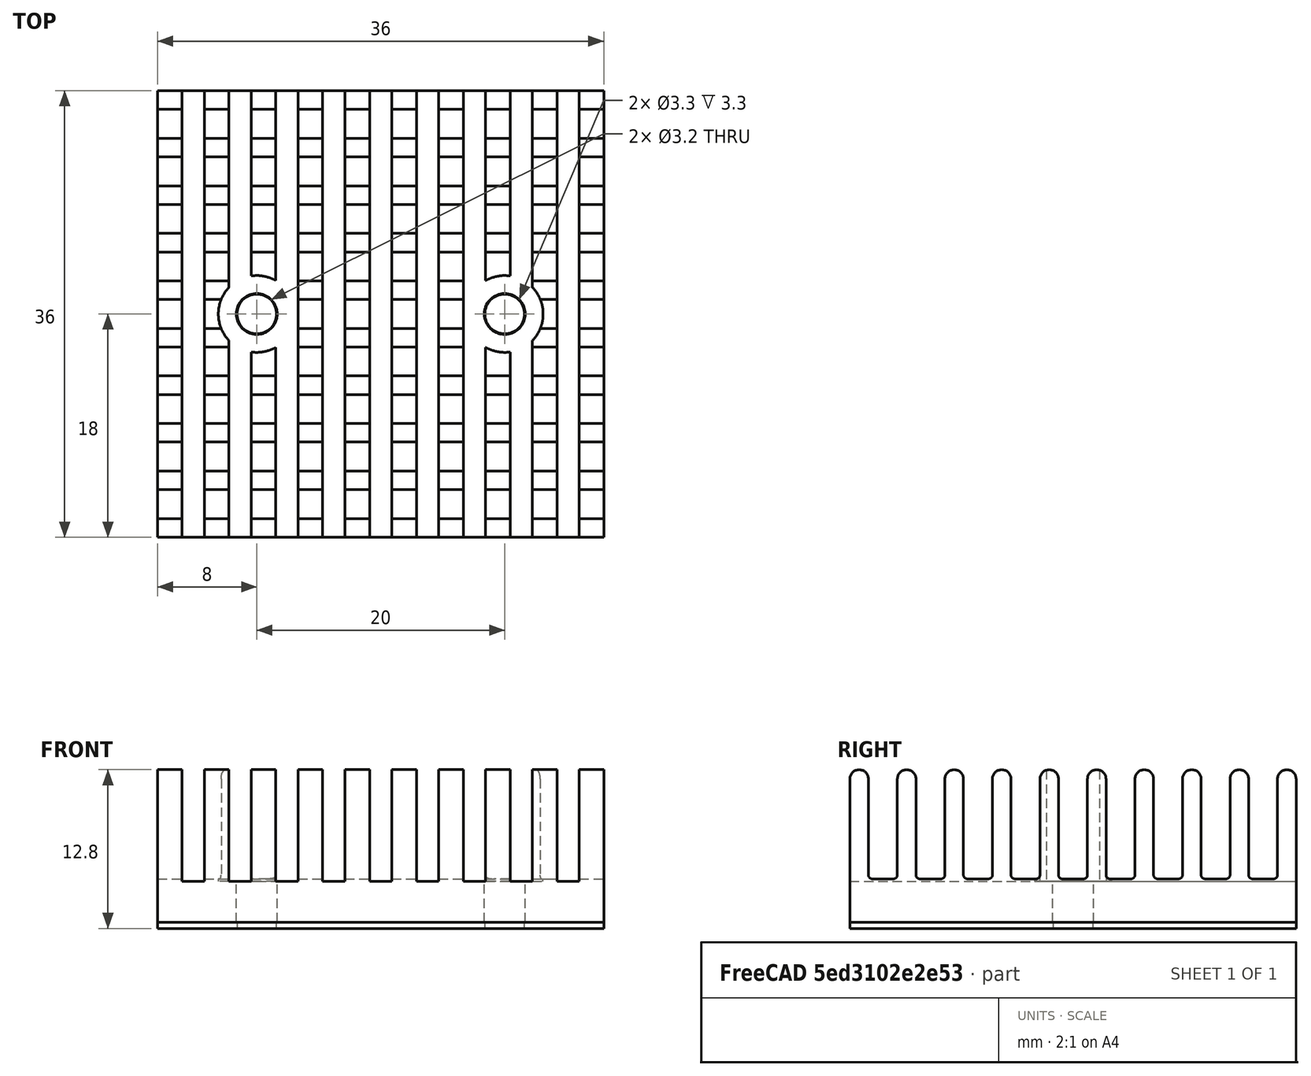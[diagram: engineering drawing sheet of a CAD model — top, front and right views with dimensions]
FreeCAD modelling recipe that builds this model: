
FCSTD DOCUMENT  (FreeCAD 0.19R)
Label: HeatSink_FischerElektronik__ICK_PGA_14_x_14_x_12
License: All rights reserved
LicenseURL: http://en.wikipedia.org/wiki/All_rights_reserved
objects: TechDraw::DrawViewDimension×11, Sketcher::SketchObject×8, App::Part×4, TechDraw::DrawProjGroupItem×4, PartDesign::Pad×3, PartDesign::Pocket×3, PartDesign::Body×3, PartDesign::Hole×2, TechDraw::DrawSVGTemplate×2, TechDraw::DrawViewAnnotation×2, TechDraw::DrawPage×2, PartDesign::Fillet×1, TechDraw::DrawProjGroup×1, TechDraw::DrawViewSection×1, TechDraw::DrawViewPart×1, PartDesign::FeatureBase×1, TechDraw::DrawViewImage×1
note: 30 computed .brp shape members not serialized (recipe doc carries the construction recipe); baked Part::Feature solids carry a one-line shape summary decoded from their .brp

FEATURE [Sketcher::SketchObject] Sketch  label="Sketch_profile"
  MapMode = 5
  Placement = pos=(0,0,0) rot=(0.57735,0.57735,0.57735;2.0944rad)
  Support = -> [YZ_Plane001]
  sketch-geometry (59):
    g0: LineSegment StartX=-18 StartY=0 StartZ=0 EndX=18 EndY=0 EndZ=0
    g1: ArcOfCircle CenterX=-17.25 CenterY=11.55 CenterZ=0 NormalX=0 NormalY=0 NormalZ=1 AngleXU=0 Radius=0.75 StartAngle=1.09717e-07 EndAngle=3.14159
    g2: LineSegment StartX=-16.5 StartY=11.55 StartZ=0 EndX=-16.5 EndY=3.5 EndZ=0
    g3: LineSegment StartX=-16.5 StartY=3.5 StartZ=0 EndX=-14.1667 EndY=3.5 EndZ=0
    g4: LineSegment StartX=-18 StartY=11.55 StartZ=0 EndX=-18 EndY=0 EndZ=0
    g5: LineSegment [constr] StartX=-17.25 StartY=11.55 StartZ=0 EndX=-17.25 EndY=12.3 EndZ=0
    g6: ArcOfCircle CenterX=-13.4167 CenterY=11.55 CenterZ=0 NormalX=0 NormalY=0 NormalZ=1 AngleXU=0 Radius=0.75 StartAngle=6.1363e-08 EndAngle=3.14159
    g7: LineSegment StartX=-12.6667 StartY=11.55 StartZ=0 EndX=-12.6667 EndY=3.5 EndZ=0
    g8: LineSegment StartX=-12.6667 StartY=3.5 StartZ=0 EndX=-10.3333 EndY=3.5 EndZ=0
    g9: LineSegment StartX=-14.1667 StartY=11.55 StartZ=0 EndX=-14.1667 EndY=3.5 EndZ=0
    g10: LineSegment [constr] StartX=-13.4167 StartY=11.55 StartZ=0 EndX=-13.4167 EndY=12.3 EndZ=0
    g11: LineSegment [constr] StartX=-16.5 StartY=11.55 StartZ=0 EndX=-12.6667 EndY=11.55 EndZ=0
    g12: ArcOfCircle CenterX=-9.58333 CenterY=11.55 CenterZ=0 NormalX=0 NormalY=0 NormalZ=1 AngleXU=0 Radius=0.75 StartAngle=6.28319 EndAngle=9.42478
    g13: LineSegment StartX=-8.83333 StartY=11.55 StartZ=0 EndX=-8.83333 EndY=3.5 EndZ=0
    g14: LineSegment StartX=-8.83333 StartY=3.5 StartZ=0 EndX=-6.5 EndY=3.5 EndZ=0
    g15: LineSegment StartX=-10.3333 StartY=11.55 StartZ=0 EndX=-10.3333 EndY=3.5 EndZ=0
    g16: LineSegment [constr] StartX=-9.58333 StartY=11.55 StartZ=0 EndX=-9.58333 EndY=12.3 EndZ=0
    g17: LineSegment [constr] StartX=-12.6667 StartY=11.55 StartZ=0 EndX=-8.83333 EndY=11.55 EndZ=0
    g18: ArcOfCircle CenterX=-5.75 CenterY=11.55 CenterZ=0 NormalX=0 NormalY=0 NormalZ=1 AngleXU=0 Radius=0.75 StartAngle=6.28319 EndAngle=9.42478
    g19: LineSegment StartX=-5 StartY=11.55 StartZ=0 EndX=-5 EndY=3.5 EndZ=0
    g20: LineSegment StartX=-5 StartY=3.5 StartZ=0 EndX=-2.66667 EndY=3.5 EndZ=0
    g21: LineSegment StartX=-6.5 StartY=11.55 StartZ=0 EndX=-6.5 EndY=3.5 EndZ=0
    g22: LineSegment [constr] StartX=-5.75 StartY=11.55 StartZ=0 EndX=-5.75 EndY=12.3 EndZ=0
    g23: LineSegment [constr] StartX=-8.83333 StartY=11.55 StartZ=0 EndX=-5 EndY=11.55 EndZ=0
    g24: ArcOfCircle CenterX=-1.91667 CenterY=11.55 CenterZ=0 NormalX=0 NormalY=0 NormalZ=1 AngleXU=0 Radius=0.75 StartAngle=5.6678e-08 EndAngle=3.14159
    g25: LineSegment StartX=-1.16667 StartY=11.55 StartZ=0 EndX=-1.16667 EndY=3.5 EndZ=0
    g26: LineSegment StartX=-1.16667 StartY=3.5 StartZ=0 EndX=1.16667 EndY=3.5 EndZ=0
    g27: LineSegment StartX=-2.66667 StartY=11.55 StartZ=0 EndX=-2.66667 EndY=3.5 EndZ=0
    g28: LineSegment [constr] StartX=-1.91667 StartY=11.55 StartZ=0 EndX=-1.91667 EndY=12.3 EndZ=0
    g29: LineSegment [constr] StartX=-5 StartY=11.55 StartZ=0 EndX=-1.16667 EndY=11.55 EndZ=0
    g30: ArcOfCircle CenterX=1.91667 CenterY=11.55 CenterZ=0 NormalX=0 NormalY=0 NormalZ=1 AngleXU=0 Radius=0.75 StartAngle=4.771e-09 EndAngle=3.14159
    g31: LineSegment StartX=2.66667 StartY=11.55 StartZ=0 EndX=2.66667 EndY=3.5 EndZ=0
    g32: LineSegment StartX=2.66667 StartY=3.5 StartZ=0 EndX=5 EndY=3.5 EndZ=0
    g33: LineSegment StartX=1.16667 StartY=11.55 StartZ=0 EndX=1.16667 EndY=3.5 EndZ=0
    g34: LineSegment [constr] StartX=1.91667 StartY=11.55 StartZ=0 EndX=1.91667 EndY=12.3 EndZ=0
    g35: LineSegment [constr] StartX=-1.16667 StartY=11.55 StartZ=0 EndX=2.66667 EndY=11.55 EndZ=0
    g36: ArcOfCircle CenterX=5.75 CenterY=11.55 CenterZ=0 NormalX=0 NormalY=0 NormalZ=1 AngleXU=0 Radius=0.75 StartAngle=2.3161e-08 EndAngle=3.1416
    g37: LineSegment StartX=6.5 StartY=11.55 StartZ=0 EndX=6.5 EndY=3.5 EndZ=0
    g38: LineSegment StartX=6.5 StartY=3.5 StartZ=0 EndX=8.83333 EndY=3.5 EndZ=0
    g39: LineSegment StartX=5 StartY=11.55 StartZ=0 EndX=5 EndY=3.5 EndZ=0
    g40: LineSegment [constr] StartX=5.75 StartY=11.55 StartZ=0 EndX=5.75 EndY=12.3 EndZ=0
    g41: LineSegment [constr] StartX=2.66667 StartY=11.55 StartZ=0 EndX=6.5 EndY=11.55 EndZ=0
    g42: ArcOfCircle CenterX=9.58333 CenterY=11.55 CenterZ=0 NormalX=0 NormalY=0 NormalZ=1 AngleXU=0 Radius=0.75 StartAngle=6.28319 EndAngle=9.42478
    g43: LineSegment StartX=10.3333 StartY=11.55 StartZ=0 EndX=10.3333 EndY=3.5 EndZ=0
    g44: LineSegment StartX=10.3333 StartY=3.5 StartZ=0 EndX=12.6667 EndY=3.5 EndZ=0
    g45: LineSegment StartX=8.83333 StartY=11.55 StartZ=0 EndX=8.83333 EndY=3.5 EndZ=0
    g46: LineSegment [constr] StartX=9.58333 StartY=11.55 StartZ=0 EndX=9.58333 EndY=12.3 EndZ=0
    g47: LineSegment [constr] StartX=6.5 StartY=11.55 StartZ=0 EndX=10.3333 EndY=11.55 EndZ=0
    g48: ArcOfCircle CenterX=13.4167 CenterY=11.55 CenterZ=0 NormalX=0 NormalY=0 NormalZ=1 AngleXU=0 Radius=0.75 StartAngle=8.3908e-08 EndAngle=3.14159
    g49: LineSegment StartX=14.1667 StartY=11.55 StartZ=0 EndX=14.1667 EndY=3.5 EndZ=0
    g50: LineSegment StartX=14.1667 StartY=3.5 StartZ=0 EndX=16.5 EndY=3.5 EndZ=0
    g51: LineSegment StartX=12.6667 StartY=11.55 StartZ=0 EndX=12.6667 EndY=3.5 EndZ=0
    g52: LineSegment [constr] StartX=13.4167 StartY=11.55 StartZ=0 EndX=13.4167 EndY=12.3 EndZ=0
    g53: LineSegment [constr] StartX=10.3333 StartY=11.55 StartZ=0 EndX=14.1667 EndY=11.55 EndZ=0
    g54: ArcOfCircle CenterX=17.25 CenterY=11.55 CenterZ=0 NormalX=0 NormalY=0 NormalZ=1 AngleXU=0 Radius=0.75 StartAngle=6.28319 EndAngle=9.42478
    g55: LineSegment StartX=18 StartY=11.55 StartZ=0 EndX=18 EndY=0 EndZ=0
    g56: LineSegment StartX=16.5 StartY=11.55 StartZ=0 EndX=16.5 EndY=3.5 EndZ=0
    g57: LineSegment [constr] StartX=17.25 StartY=11.55 StartZ=0 EndX=17.25 EndY=12.3 EndZ=0
    g58: LineSegment [constr] StartX=14.1667 StartY=11.55 StartZ=0 EndX=18 EndY=11.55 EndZ=0
  constraints (177):
    c: Horizontal(g0)
    c: Symmetric(g0,g0,g-1)
    c: DistanceX(g0,g0) = 36
    c: Vertical(g2)
    c: Coincident(g3,g2)
    c: Horizontal(g3)
    c: Coincident(g1,g2)
    c: Tangent(g1,g2)
    c: Coincident(g4,g1)
    c: Vertical(g4)
    c: Tangent(g4,g1)
    c: Vertical(g5)
    c: Coincident(g1,g5)
    c: PointOnObject(g5,g1)
    c: DistanceY(g0,g5) = 12.3
    c: DistanceY(g0,g2) = 3.5
    c: Radius(g1) = 0.75
    c: Vertical(g7)
    c: Coincident(g8,g7)
    c: Horizontal(g8)
    c: Coincident(g6,g7)
    c: Tangent(g6,g7)
    c: Coincident(g9,g6)
    c: Vertical(g9)
    c: Tangent(g9,g6)
    c: Equal(g9,g7)
    c: Vertical(g10)
    c: Coincident(g6,g10)
    c: PointOnObject(g10,g6)
    c: Equal(g1,g6) = 0.75
    c: Coincident(g1,g11)
    c: Coincident(g6,g11)
    c: Vertical(g13)
    c: Coincident(g14,g13)
    c: Horizontal(g14)
    c: Coincident(g12,g13)
    c: Tangent(g12,g13)
    c: Coincident(g15,g12)
    c: Vertical(g15)
    c: Tangent(g15,g12)
    c: Equal(g15,g13)
    c: Vertical(g16)
    c: Coincident(g12,g16)
    c: PointOnObject(g16,g12)
    c: Equal(g1,g12) = 0.75
    c: Coincident(g6,g17)
    c: Coincident(g12,g17)
    c: Equal(g11,g17)
    c: Parallel(g17,g11)
    c: Vertical(g19)
    c: Coincident(g20,g19)
    c: Horizontal(g20)
    c: Coincident(g18,g19)
    c: Tangent(g18,g19)
    c: Coincident(g21,g18)
    c: Vertical(g21)
    c: Tangent(g21,g18)
    c: Equal(g21,g19)
    c: Vertical(g22)
    c: Coincident(g18,g22)
    c: PointOnObject(g22,g18)
    c: Equal(g1,g18) = 0.75
    c: Coincident(g12,g23)
    c: Coincident(g18,g23)
    c: Equal(g11,g23)
    c: Parallel(g23,g11)
    c: Vertical(g25)
    c: Coincident(g26,g25)
    c: Horizontal(g26)
    c: Coincident(g24,g25)
    c: Tangent(g24,g25)
    c: Coincident(g27,g24)
    c: Vertical(g27)
    c: Tangent(g27,g24)
    c: Equal(g27,g25)
    c: Vertical(g28)
    c: Coincident(g24,g28)
    c: PointOnObject(g28,g24)
    c: Equal(g1,g24) = 0.75
    c: Coincident(g18,g29)
    c: Coincident(g24,g29)
    c: Equal(g11,g29)
    c: Parallel(g29,g11)
    c: Vertical(g31)
    c: Coincident(g32,g31)
    c: Horizontal(g32)
    c: Coincident(g30,g31)
    c: Tangent(g30,g31)
    c: Coincident(g33,g30)
    c: Vertical(g33)
    c: Tangent(g33,g30)
    c: Equal(g33,g31)
    c: Vertical(g34)
    c: Coincident(g30,g34)
    c: PointOnObject(g34,g30)
    c: Equal(g1,g30) = 0.75
    c: Coincident(g24,g35)
    c: Coincident(g30,g35)
    c: Equal(g11,g35)
    c: Parallel(g35,g11)
    c: Vertical(g37)
    c: Coincident(g38,g37)
    c: Horizontal(g38)
    c: Coincident(g36,g37)
    c: Tangent(g36,g37)
    c: Coincident(g39,g36)
    c: Vertical(g39)
    c: Tangent(g39,g36)
    c: Equal(g39,g37)
    c: Vertical(g40)
    c: Coincident(g36,g40)
    c: PointOnObject(g40,g36)
    c: Equal(g1,g36) = 0.75
    c: Coincident(g30,g41)
    c: Coincident(g36,g41)
    c: Equal(g11,g41)
    c: Parallel(g41,g11)
    c: Vertical(g43)
    c: Coincident(g44,g43)
    c: Horizontal(g44)
    c: Coincident(g42,g43)
    c: Tangent(g42,g43)
    c: Coincident(g45,g42)
    c: Vertical(g45)
    c: Tangent(g45,g42)
    c: Equal(g45,g43)
    c: Vertical(g46)
    c: Coincident(g42,g46)
    c: PointOnObject(g46,g42)
    c: Equal(g1,g42) = 0.75
    c: Coincident(g36,g47)
    c: Coincident(g42,g47)
    c: Equal(g11,g47)
    c: Parallel(g47,g11)
    c: Vertical(g49)
    c: Coincident(g50,g49)
    c: Horizontal(g50)
    c: Coincident(g48,g49)
    c: Tangent(g48,g49)
    c: Coincident(g51,g48)
    c: Vertical(g51)
    c: Tangent(g51,g48)
    c: Equal(g51,g49)
    c: Vertical(g52)
    c: Coincident(g48,g52)
    c: PointOnObject(g52,g48)
    c: Equal(g1,g48) = 0.75
    c: Coincident(g42,g53)
    c: Coincident(g48,g53)
    c: Equal(g11,g53)
    c: Parallel(g53,g11)
    c: Vertical(g55)
    c: Coincident(g54,g55)
    c: Tangent(g54,g55)
    c: Coincident(g56,g54)
    c: Vertical(g56)
    c: Tangent(g56,g54)
    c: Vertical(g57)
    c: Coincident(g54,g57)
    c: PointOnObject(g57,g54)
    c: Equal(g1,g54) = 0.75
    c: Coincident(g48,g58)
    c: Coincident(g54,g58)
    c: Equal(g11,g58)
    c: Parallel(g58,g11)
    c: Horizontal(g11)
    c: Coincident(g3,g9)
    c: Coincident(g8,g15)
    c: Coincident(g14,g21)
    c: Coincident(g20,g27)
    c: Coincident(g26,g33)
    c: Coincident(g32,g39)
    c: Coincident(g38,g45)
    c: Coincident(g44,g51)
    c: Coincident(g50,g56)
    c: Coincident(g55,g0)
    c: Coincident(g4,g0)
FEATURE [PartDesign::Pad] Pad  label="Pad_profile"
  AllowMultiFace = false
  Direction = (1,1,1)
  Length = 36
  Length2 = 100
  Midplane = true
  Placement = pos=(0,0,0) rot=(0.57735,0.57735,0.57735;2.0944rad)
  Profile = -> Sketch
  Type = 0
FEATURE [Sketcher::SketchObject] Sketch001  label="Sketch_cuts"
  ExternalGeometry = -> [Pad]
  MapMode = 5
  Placement = pos=(0,-18,2e-15) rot=(0.57735,0.57735,-0.57735;2.0944rad)
  Support = -> [Pad]
  sketch-geometry (47):
    g0: LineSegment StartX=-13.55 StartY=16.02 StartZ=0 EndX=-3.3 EndY=16.02 EndZ=0
    g1: LineSegment StartX=-3.3 StartY=16.02 StartZ=0 EndX=-3.3 EndY=14.22 EndZ=0
    g2: LineSegment StartX=-3.3 StartY=14.22 StartZ=0 EndX=-13.55 EndY=14.22 EndZ=0
    g3: LineSegment StartX=-13.55 StartY=14.22 StartZ=0 EndX=-13.55 EndY=16.02 EndZ=0
    g4: LineSegment [constr] StartX=-3.3 StartY=16.02 StartZ=0 EndX=-3.3 EndY=18 EndZ=0
    g5: LineSegment StartX=-13.55 StartY=12.24 StartZ=0 EndX=-3.3 EndY=12.24 EndZ=0
    g6: LineSegment StartX=-3.3 StartY=12.24 StartZ=0 EndX=-3.3 EndY=10.44 EndZ=0
    g7: LineSegment StartX=-3.3 StartY=10.44 StartZ=0 EndX=-13.55 EndY=10.44 EndZ=0
    g8: LineSegment StartX=-13.55 StartY=10.44 StartZ=0 EndX=-13.55 EndY=12.24 EndZ=0
    g9: LineSegment [constr] StartX=-13.55 StartY=16.02 StartZ=0 EndX=-13.55 EndY=12.24 EndZ=0
    g10: LineSegment StartX=-13.55 StartY=8.46 StartZ=0 EndX=-3.3 EndY=8.46 EndZ=0
    g11: LineSegment StartX=-3.3 StartY=8.46 StartZ=0 EndX=-3.3 EndY=6.66 EndZ=0
    g12: LineSegment StartX=-3.3 StartY=6.66 StartZ=0 EndX=-13.55 EndY=6.66 EndZ=0
    g13: LineSegment StartX=-13.55 StartY=6.66 StartZ=0 EndX=-13.55 EndY=8.46 EndZ=0
    g14: LineSegment [constr] StartX=-13.55 StartY=12.24 StartZ=0 EndX=-13.55 EndY=8.46 EndZ=0
    g15: LineSegment StartX=-13.55 StartY=4.68 StartZ=0 EndX=-3.3 EndY=4.68 EndZ=0
    g16: LineSegment StartX=-3.3 StartY=4.68 StartZ=0 EndX=-3.3 EndY=2.88 EndZ=0
    g17: LineSegment StartX=-3.3 StartY=2.88 StartZ=0 EndX=-13.55 EndY=2.88 EndZ=0
    g18: LineSegment StartX=-13.55 StartY=2.88 StartZ=0 EndX=-13.55 EndY=4.68 EndZ=0
    g19: LineSegment [constr] StartX=-13.55 StartY=8.46 StartZ=0 EndX=-13.55 EndY=4.68 EndZ=0
    g20: LineSegment StartX=-13.55 StartY=0.9 StartZ=0 EndX=-3.3 EndY=0.9 EndZ=0
    g21: LineSegment StartX=-3.3 StartY=0.9 StartZ=0 EndX=-3.3 EndY=-0.9 EndZ=0
    g22: LineSegment StartX=-3.3 StartY=-0.9 StartZ=0 EndX=-13.55 EndY=-0.9 EndZ=0
    g23: LineSegment StartX=-13.55 StartY=-0.9 StartZ=0 EndX=-13.55 EndY=0.9 EndZ=0
    g24: LineSegment [constr] StartX=-13.55 StartY=4.68 StartZ=0 EndX=-13.55 EndY=0.9 EndZ=0
    g25: LineSegment StartX=-13.55 StartY=-2.88 StartZ=0 EndX=-3.3 EndY=-2.88 EndZ=0
    g26: LineSegment StartX=-3.3 StartY=-2.88 StartZ=0 EndX=-3.3 EndY=-4.68 EndZ=0
    g27: LineSegment StartX=-3.3 StartY=-4.68 StartZ=0 EndX=-13.55 EndY=-4.68 EndZ=0
    g28: LineSegment StartX=-13.55 StartY=-4.68 StartZ=0 EndX=-13.55 EndY=-2.88 EndZ=0
    g29: LineSegment [constr] StartX=-13.55 StartY=0.9 StartZ=0 EndX=-13.55 EndY=-2.88 EndZ=0
    g30: LineSegment StartX=-13.55 StartY=-6.66 StartZ=0 EndX=-3.3 EndY=-6.66 EndZ=0
    g31: LineSegment StartX=-3.3 StartY=-6.66 StartZ=0 EndX=-3.3 EndY=-8.46 EndZ=0
    g32: LineSegment StartX=-3.3 StartY=-8.46 StartZ=0 EndX=-13.55 EndY=-8.46 EndZ=0
    g33: LineSegment StartX=-13.55 StartY=-8.46 StartZ=0 EndX=-13.55 EndY=-6.66 EndZ=0
    g34: LineSegment [constr] StartX=-13.55 StartY=-2.88 StartZ=0 EndX=-13.55 EndY=-6.66 EndZ=0
    g35: LineSegment StartX=-13.55 StartY=-10.44 StartZ=0 EndX=-3.3 EndY=-10.44 EndZ=0
    g36: LineSegment StartX=-3.3 StartY=-10.44 StartZ=0 EndX=-3.3 EndY=-12.24 EndZ=0
    g37: LineSegment StartX=-3.3 StartY=-12.24 StartZ=0 EndX=-13.55 EndY=-12.24 EndZ=0
    g38: LineSegment StartX=-13.55 StartY=-12.24 StartZ=0 EndX=-13.55 EndY=-10.44 EndZ=0
    g39: LineSegment [constr] StartX=-13.55 StartY=-6.66 StartZ=0 EndX=-13.55 EndY=-10.44 EndZ=0
    g40: LineSegment StartX=-13.55 StartY=-14.22 StartZ=0 EndX=-3.3 EndY=-14.22 EndZ=0
    g41: LineSegment StartX=-3.3 StartY=-14.22 StartZ=0 EndX=-3.3 EndY=-16.02 EndZ=0
    g42: LineSegment StartX=-3.3 StartY=-16.02 StartZ=0 EndX=-13.55 EndY=-16.02 EndZ=0
    g43: LineSegment StartX=-13.55 StartY=-16.02 StartZ=0 EndX=-13.55 EndY=-14.22 EndZ=0
    g44: LineSegment [constr] StartX=-13.55 StartY=-10.44 StartZ=0 EndX=-13.55 EndY=-14.22 EndZ=0
    g45: LineSegment [constr] StartX=-3.3 StartY=14.22 StartZ=0 EndX=-3.3 EndY=12.24 EndZ=0
    g46: LineSegment [constr] StartX=-3.3 StartY=-16.02 StartZ=0 EndX=-3.3 EndY=-18 EndZ=0
  constraints (132):
    c: Coincident(g0,g1)
    c: Coincident(g1,g2)
    c: Coincident(g2,g3)
    c: Coincident(g3,g0)
    c: Horizontal(g0)
    c: Horizontal(g2)
    c: Vertical(g1)
    c: Vertical(g3)
    c: DistanceX(g0,g-3) = 2
    c: DistanceX(g0,g-3) = 3.3
    c: Vertical(g4)
    c: Coincident(g0,g4)
    c: DistanceY(g1,g1) = 1.8
    c: PointOnObject(g4,g-3)
    c: Coincident(g5,g6)
    c: Coincident(g6,g7)
    c: Coincident(g7,g8)
    c: Coincident(g8,g5)
    c: Horizontal(g5)
    c: Horizontal(g7)
    c: Vertical(g6)
    c: Vertical(g8)
    c: Equal(g1,g6) = 1.8
    c: Coincident(g0,g9)
    c: Coincident(g5,g9)
    c: Coincident(g10,g11)
    c: Coincident(g11,g12)
    c: Coincident(g12,g13)
    c: Coincident(g13,g10)
    c: Horizontal(g10)
    c: Horizontal(g12)
    c: Vertical(g11)
    c: Vertical(g13)
    c: Equal(g1,g11) = 1.8
    c: Coincident(g5,g14)
    c: Coincident(g10,g14)
    c: Equal(g9,g14)
    c: Parallel(g14,g9)
    c: Coincident(g15,g16)
    c: Coincident(g16,g17)
    c: Coincident(g17,g18)
    c: Coincident(g18,g15)
    c: Horizontal(g15)
    c: Horizontal(g17)
    c: Vertical(g16)
    c: Vertical(g18)
    c: Equal(g1,g16) = 1.8
    c: Coincident(g10,g19)
    c: Coincident(g15,g19)
    c: Equal(g9,g19)
    c: Parallel(g19,g9)
    c: Coincident(g20,g21)
    c: Coincident(g21,g22)
    c: Coincident(g22,g23)
    c: Coincident(g23,g20)
    c: Horizontal(g20)
    c: Horizontal(g22)
    c: Vertical(g21)
    c: Vertical(g23)
    c: Equal(g1,g21) = 1.8
    c: Coincident(g15,g24)
    c: Coincident(g20,g24)
    c: Equal(g9,g24)
    c: Parallel(g24,g9)
    c: Coincident(g25,g26)
    c: Coincident(g26,g27)
    c: Coincident(g27,g28)
    c: Coincident(g28,g25)
    c: Horizontal(g25)
    c: Horizontal(g27)
    c: Vertical(g26)
    c: Vertical(g28)
    c: Equal(g1,g26) = 1.8
    c: Coincident(g20,g29)
    c: Coincident(g25,g29)
    c: Equal(g9,g29)
    c: Parallel(g29,g9)
    c: Coincident(g30,g31)
    c: Coincident(g31,g32)
    c: Coincident(g32,g33)
    c: Coincident(g33,g30)
    c: Horizontal(g30)
    c: Horizontal(g32)
    c: Vertical(g31)
    c: Vertical(g33)
    c: Equal(g1,g31) = 1.8
    c: Coincident(g25,g34)
    c: Coincident(g30,g34)
    c: Equal(g9,g34)
    c: Parallel(g34,g9)
    c: Coincident(g35,g36)
    c: Coincident(g36,g37)
    c: Coincident(g37,g38)
    c: Coincident(g38,g35)
    c: Horizontal(g35)
    c: Horizontal(g37)
    c: Vertical(g36)
    c: Vertical(g38)
    c: Equal(g1,g36) = 1.8
    c: Coincident(g30,g39)
    c: Coincident(g35,g39)
    c: Equal(g9,g39)
    c: Parallel(g39,g9)
    c: Coincident(g40,g41)
    c: Coincident(g41,g42)
    c: Coincident(g42,g43)
    c: Coincident(g43,g40)
    c: Horizontal(g40)
    c: Horizontal(g42)
    c: Vertical(g41)
    c: Vertical(g43)
    c: Equal(g1,g41) = 1.8
    c: Coincident(g35,g44)
    c: Coincident(g40,g44)
    c: Equal(g9,g44)
    c: Parallel(g44,g9)
    c: Vertical(g9)
    c: Vertical(g45)
    c: Coincident(g45,g1)
    c: Coincident(g5,g45)
    c: Equal(g45,g4)
    c: PointOnObject(g10,g6)
    c: PointOnObject(g15,g6)
    c: PointOnObject(g20,g6)
    c: PointOnObject(g25,g6)
    c: PointOnObject(g30,g6)
    c: PointOnObject(g35,g6)
    c: Vertical(g46)
    c: PointOnObject(g46,g-4)
    c: Coincident(g41,g46)
    c: PointOnObject(g40,g6)
    c: Equal(g4,g46)
FEATURE [PartDesign::Fillet] Fillet
  Base = -> Pad [Edge113,Edge116,Edge104,Edge101,Edge89,Edge77,Edge65,Edge53,Edge41,Edge29,Edge17,Edge92,Edge80,Edge68,Edge56,Edge44,Edge32,Edge20]
  BaseFeature = -> Pad
  Placement = pos=(0,0,0) rot=(0.57735,0.57735,0.57735;2.0944rad)
  Radius = 0.3
  SupportTransform = false
FEATURE [PartDesign::Pocket] Pocket  label="Pocket_cut"
  AllowMultiFace = false
  BaseFeature = -> Fillet
  Length = 5
  Length2 = 100
  Placement = pos=(0,0,0) rot=(0.57735,0.57735,0.57735;2.0944rad)
  Profile = -> Sketch001
  Type = 1
FEATURE [Sketcher::SketchObject] Sketch002  label="sketch_hole_M3"
  MapMode = 5
  Placement = pos=(0,0,0) rot=(0.707107,0.707107,0;3.14159rad)
  Support = -> [Pocket]
  sketch-geometry (3):
    g0: Circle CenterX=0 CenterY=10 CenterZ=0 NormalX=0 NormalY=0 NormalZ=1 AngleXU=0 Radius=1
    g1: Circle CenterX=0 CenterY=-10 CenterZ=0 NormalX=0 NormalY=0 NormalZ=1 AngleXU=0 Radius=1
    g2: LineSegment [constr] StartX=0 StartY=10 StartZ=0 EndX=0 EndY=-10 EndZ=0
  constraints (7):
    c: Equal(g1,g0)
    c: Coincident(g0,g2)
    c: Coincident(g1,g2)
    c: Vertical(g2)
    c: Symmetric(g2,g2,g-1)
    c: DistanceY(g2,g2) = 20
    c: Diameter(g0) = 2
FEATURE [Sketcher::SketchObject] Sketch003  label="foil_base"
  MapMode = 5
  Support = -> [XY_Plane003]
  sketch-geometry (4):
    g0: LineSegment StartX=-18 StartY=-18 StartZ=0 EndX=18 EndY=-18 EndZ=0
    g1: LineSegment StartX=18 StartY=-18 StartZ=0 EndX=18 EndY=18 EndZ=0
    g2: LineSegment StartX=18 StartY=18 StartZ=0 EndX=-18 EndY=18 EndZ=0
    g3: LineSegment StartX=-18 StartY=18 StartZ=0 EndX=-18 EndY=-18 EndZ=0
  constraints (11):
    c: Coincident(g0,g1)
    c: Coincident(g1,g2)
    c: Coincident(g2,g3)
    c: Coincident(g3,g0)
    c: Horizontal(g0)
    c: Horizontal(g2)
    c: Vertical(g1)
    c: Vertical(g3)
    c: Equal(g0,g1)
    c: Symmetric(g1,g0,g-1)
    c: DistanceY(g1,g1) = 36
FEATURE [PartDesign::Pad] Pad001  label="Pad_foil"
  AllowMultiFace = false
  Direction = (1,1,1)
  Length = 0.5
  Length2 = 100
  Profile = -> Sketch003
  Reversed = true
  Type = 0
FEATURE [Sketcher::SketchObject] Sketch004
  MapMode = 5
  Placement = pos=(0,0,-0.5) rot=(1,0,0;3.14159rad)
  Support = -> [Pad001]
  sketch-geometry (3):
    g0: LineSegment [constr] StartX=-10 StartY=0 StartZ=0 EndX=10 EndY=0 EndZ=0
    g1: Circle CenterX=-10 CenterY=0 CenterZ=0 NormalX=0 NormalY=0 NormalZ=1 AngleXU=0 Radius=1.6
    g2: Circle CenterX=10 CenterY=0 CenterZ=0 NormalX=0 NormalY=0 NormalZ=1 AngleXU=0 Radius=1.6
  constraints (7):
    c: Equal(g1,g2)
    c: Coincident(g1,g0)
    c: Coincident(g0,g2)
    c: Radius(g1) = 1.6
    c: Horizontal(g0)
    c: DistanceX(g0,g0) = 20
    c: Symmetric(g0,g0,g-1)
FEATURE [PartDesign::Pocket] Pocket002  label="Pocket_screwholes_3,2mm"
  AllowMultiFace = false
  BaseFeature = -> Pad001
  Length = 5
  Length2 = 100
  Profile = -> Sketch004
  Type = 1
FEATURE [PartDesign::Body] Body001  label="thermal_foil"
  Group = -> [Sketch003,Pad001,Sketch004,Pocket002]
  Origin = -> Origin003
  Tip = -> Pocket002
FEATURE [App::Part] Part001  label="thermally conductive foil cutting"
  Group = -> [Body001]
  License = CC BY 4.0
  LicenseURL = http://creativecommons.org/licenses/by/4.0/
  Origin = -> Origin002
FEATURE [Sketcher::SketchObject] Sketch005  label="Sketch_Hex_10"
  MapMode = 5
  Support = -> [XY_Plane005]
  sketch-geometry (7):
    g0: LineSegment StartX=1.44338 StartY=2.5 StartZ=0 EndX=-1.44338 EndY=2.5 EndZ=0
    g1: LineSegment StartX=-1.44338 StartY=2.5 StartZ=0 EndX=-2.88675 EndY=0 EndZ=0
    g2: LineSegment StartX=-2.88675 StartY=0 StartZ=0 EndX=-1.44338 EndY=-2.5 EndZ=0
    g3: LineSegment StartX=-1.44338 StartY=-2.5 StartZ=0 EndX=1.44338 EndY=-2.5 EndZ=0
    g4: LineSegment StartX=1.44338 StartY=-2.5 StartZ=0 EndX=2.88675 EndY=0 EndZ=0
    g5: LineSegment StartX=2.88675 StartY=0 StartZ=0 EndX=1.44338 EndY=2.5 EndZ=0
    g6: Circle [constr] CenterX=0 CenterY=0 CenterZ=0 NormalX=0 NormalY=0 NormalZ=1 AngleXU=0 Radius=2.88675
  constraints (16):
    c: Coincident(g0,g1)
    c: Coincident(g1,g2)
    c: Coincident(g2,g3)
    c: Coincident(g3,g4)
    c: Coincident(g4,g5)
    c: Coincident(g5,g0)
    c: Equal(g0, g1-g5) x5
    c: PointOnObject(g0,g6)
    c: PointOnObject(g1,g6)
    c: PointOnObject(g2,g6)
    c: PointOnObject(g3,g6)
    c: PointOnObject(g4,g6)
    c: PointOnObject(g5,g6)
    c: Coincident(g6,g-1)
    c: Horizontal(g0)
    c: DistanceY(g3,g0) = 5
FEATURE [PartDesign::Pad] Pad002  label="Pad_Hex"
  AllowMultiFace = false
  Direction = (1,1,1)
  Length = 15
  Length2 = 100
  Profile = -> Sketch005
  Type = 0
FEATURE [Sketcher::SketchObject] Sketch006  label="Sketch_Hex_M3"
  MapMode = 5
  Placement = pos=(0,0,15) rot=(0,0,1;0rad)
  Support = -> [Pad002]
  sketch-geometry (1):
    g0: Circle CenterX=0 CenterY=0 CenterZ=0 NormalX=0 NormalY=0 NormalZ=1 AngleXU=0 Radius=1.5
  constraints (2):
    c: Coincident(g0,g-1)
    c: Radius(g0) = 1.5
FEATURE [PartDesign::Hole] Hole
  AllowMultiFace = false
  BaseFeature = -> Pad002
  Depth = 25
  DepthType = 1
  Diameter = 2.5
  DrillPoint = 1
  DrillPointAngle = 118
  HoleCutCountersinkAngle = 90
  HoleCutDepth = 0
  HoleCutDiameter = 3
  HoleCutType = 0
  ModelActualThread = false
  Profile = -> Sketch006
  Tapered = false
  TaperedAngle = 90
  ThreadAngle = 60
  ThreadClass = 0
  ThreadCutOffInner = 0.0541266
  ThreadCutOffOuter = 0.108253
  ThreadDirection = 0
  ThreadFit = 0
  ThreadPitch = 0.5
  ThreadSize = 3
  ThreadType = 1
  Threaded = true
FEATURE [PartDesign::Body] Body002  label="Body_Spacer_Hex_M3x15"
  Group = -> [Sketch005,Pad002,Sketch006,Hole]
  Origin = -> Origin005
  Placement = pos=(-10,0,3.3) rot=(0,0,1;0rad)
  Tip = -> Hole
FEATURE [App::Part] Part002  label="Spacer_Hex_M3x15"
  Group = -> [Body002]
  License = CC BY 3.0
  LicenseURL = http://creativecommons.org/licenses/by/3.0/
  Origin = -> Origin004
FEATURE [PartDesign::Hole] Hole001  label="Hole_M3"
  AllowMultiFace = false
  BaseFeature = -> Pocket
  Depth = 25
  DepthType = 1
  Diameter = 3.3
  DrillPoint = 1
  DrillPointAngle = 118
  HoleCutCountersinkAngle = 90
  HoleCutDepth = 0
  HoleCutDiameter = 3
  HoleCutType = 0
  ModelActualThread = false
  Placement = pos=(0,0,0) rot=(0.57735,0.57735,0.57735;2.0944rad)
  Profile = -> Sketch002
  Tapered = false
  TaperedAngle = 90
  ThreadAngle = 60
  ThreadClass = 0
  ThreadCutOffInner = 0.0541266
  ThreadCutOffOuter = 0.108253
  ThreadDirection = 1
  ThreadFit = 0
  ThreadPitch = 0.5
  ThreadSize = 3
  ThreadType = 1
  Threaded = false
FEATURE [Sketcher::SketchObject] Sketch007  label="sketch_place_for_spacer"
  AttachmentOffset = pos=(0,0,0) rot=(0,0,1;1.5708rad)
  MapMode = 5
  Placement = pos=(4e-16,4e-16,3.3) rot=(0,0,1;0rad)
  Support = -> [Hole001]
  sketch-geometry (3):
    g0: LineSegment [constr] StartX=-10 StartY=0 StartZ=0 EndX=10 EndY=0 EndZ=0
    g1: Circle CenterX=-10 CenterY=0 CenterZ=0 NormalX=0 NormalY=0 NormalZ=1 AngleXU=0 Radius=3.1
    g2: Circle CenterX=10 CenterY=0 CenterZ=0 NormalX=0 NormalY=0 NormalZ=1 AngleXU=0 Radius=3.1
  constraints (7):
    c: Horizontal(g0)
    c: Symmetric(g0,g0,g-1)
    c: DistanceX(g0,g0) = 20
    c: Coincident(g1,g0)
    c: Coincident(g2,g0)
    c: Equal(g1,g2)
    c: Radius(g1) = 3.1
FEATURE [PartDesign::Pocket] Pocket003  label="Pocket_place_for_spacer"
  AllowMultiFace = false
  BaseFeature = -> Hole001
  Length = 5
  Length2 = 100
  Placement = pos=(0,0,0) rot=(0.57735,0.57735,0.57735;2.0944rad)
  Profile = -> Sketch007
  Reversed = true
  Type = 1
FEATURE [PartDesign::Body] Body  label="HeatSink"
  Group = -> [Sketch,Pad,Fillet,Sketch001,Pocket,Sketch002,Hole001,Sketch007,Pocket003]
  Origin = -> Origin001
  Tip = -> Pocket003
FEATURE [App::Part] Part  label="Fischer Elektronik ICK PGA14x14x12 HeatSink"
  Group = -> [Body]
  License = CC BY 3.0
  LicenseURL = http://creativecommons.org/licenses/by/3.0/
  Origin = -> Origin
FEATURE [TechDraw::DrawSVGTemplate] Template  label="Template_Drawing_LEDBoard_4x4_16bit_HeatSink"
  EditableTexts = Designed_by_Name=Stefan Krüger; Drawing_number=1; FC-Date=20.09.2020; FC-SC=1:1; FC-SH=1; FC-Title=LEDBoard 4x4 16bit; Subtitle=HeatSink; Weight=-; extra_information_title=URL; extra_information_value=https://github.com/<owner>/LEDBoard_4x4_16bit/
  Height = 210
  Orientation = 1
  Width = 297
FEATURE [TechDraw::DrawProjGroupItem] ProjItem  label="Front"
  CoarseView = false
  Direction = (0,-1,0)
  Focus = 100
  HardHidden = false
  IsoCount = 0
  IsoHidden = false
  IsoVisible = false
  LockPosition = false
  Perspective = false
  Rotation = 0
  RotationVector = (1,0,0)
  ScaleType = 0
  SeamHidden = false
  SeamVisible = false
  SmoothHidden = false
  SmoothVisible = false
  Source = -> [Part]
  Type = 0
  X = -36.7018
  XDirection = (1,0,0)
  Y = 32.2133
FEATURE [TechDraw::DrawProjGroupItem] ProjItem003  label="Top"
  CoarseView = false
  Direction = (0,0,1)
  Focus = 100
  HardHidden = false
  IsoCount = 0
  IsoHidden = false
  IsoVisible = false
  LockPosition = false
  Perspective = false
  Rotation = 0
  RotationVector = (1,0,0)
  ScaleType = 0
  SeamHidden = false
  SeamVisible = false
  SmoothHidden = false
  SmoothVisible = false
  Source = -> [Part]
  Type = 4
  X = 0
  XDirection = (1,0,0)
  Y = -52.8848
FEATURE [TechDraw::DrawProjGroupItem] ProjItem004  label="FrontTopLeft"
  CoarseView = false
  Direction = (-1,-1,1)
  Focus = 100
  HardHidden = false
  IsoCount = 0
  IsoHidden = false
  IsoVisible = false
  LockPosition = false
  Perspective = false
  Rotation = 0
  RotationVector = (1,1,0)
  ScaleType = 0
  SeamHidden = false
  SeamVisible = false
  SmoothHidden = false
  SmoothVisible = false
  Source = -> [Part]
  Type = 6
  X = 78.6463
  XDirection = (1,1,0)
  Y = -88.0092
FEATURE [TechDraw::DrawProjGroupItem] ProjItem002  label="Bottom"
  CoarseView = false
  Direction = (0,0,-1)
  Focus = 100
  HardHidden = false
  IsoCount = 0
  IsoHidden = false
  IsoVisible = false
  LockPosition = false
  Perspective = false
  Rotation = 0
  RotationVector = (1,0,0)
  ScaleType = 0
  SeamHidden = false
  SeamVisible = false
  SmoothHidden = false
  SmoothVisible = false
  Source = -> [Part]
  Type = 5
  X = 0.830009
  XDirection = (1,0,0)
  Y = -102.299
FEATURE [TechDraw::DrawProjGroup] ProjGroup
  Anchor = -> ProjItem
  AutoDistribute = false
  LockPosition = false
  ProjectionType = 0
  Rotation = 0
  ScaleType = 0
  Source = -> [Part]
  Views = -> [ProjItem,ProjItem002,ProjItem003,ProjItem004]
  X = 77.7334
  Y = 177.725
  spacingX = 5
  spacingY = 5
FEATURE [TechDraw::DrawViewAnnotation] Annotation  label="Annotation_M3"
  Font = osifont
  LineSpace = 80
  LockPosition = false
  MaxWidth = -1
  Rotation = 0
  ScaleType = 0
  Text = for M3,  | through all
  TextSize = 3
  TextStyle = 0
  X = 115.536
  Y = 134.657
FEATURE [TechDraw::DrawViewAnnotation] Annotation002  label="Annotation_finns"
  Font = osifont
  LineSpace = 80
  LockPosition = false
  MaxWidth = -1
  Rotation = 0
  ScaleType = 0
  Text = 6.2mm drill  | (removes finns only)
  TextSize = 3
  TextStyle = 0
  X = 35.8888
  Y = 136.745
FEATURE [TechDraw::DrawViewDimension] Dimension005
  Arbitrary = false
  FormatSpec = %.3f
  Inverted = false
  LockPosition = false
  MeasureType = 1
  OverTolerance = 0
  References2D = -> [ProjItem002]
  Rotation = 0
  ScaleType = 0
  TheoreticalExact = false
  Type = 1
  UnderTolerance = 0
  X = 0.485312
  Y = 8.2503
FEATURE [TechDraw::DrawViewDimension] Dimension006
  Arbitrary = false
  FormatSpec = %.3f
  Inverted = false
  LockPosition = false
  MeasureType = 1
  OverTolerance = 0
  References2D = -> [ProjItem002]
  Rotation = 0
  ScaleType = 0
  TheoreticalExact = false
  Type = 1
  UnderTolerance = 0
  X = 5.64981
  Y = -25.6118
FEATURE [TechDraw::DrawViewDimension] Dimension007
  Arbitrary = false
  FormatSpec = %.3f
  Inverted = false
  LockPosition = false
  MeasureType = 1
  OverTolerance = 0
  References2D = -> [ProjItem002]
  Rotation = 0
  ScaleType = 0
  TheoreticalExact = false
  Type = 2
  UnderTolerance = 0
  X = -41.3511
  Y = 15.9938
FEATURE [TechDraw::DrawViewDimension] Dimension008
  Arbitrary = false
  FormatSpec = %.3f
  Inverted = false
  LockPosition = false
  MeasureType = 1
  OverTolerance = 0
  References2D = -> [ProjItem002]
  Rotation = 0
  ScaleType = 0
  TheoreticalExact = false
  Type = 1
  UnderTolerance = 0
  X = 0
  Y = 25.355
FEATURE [TechDraw::DrawViewSection] Section  label="Section A - A"
  BaseView = -> ProjItem003
  CoarseView = false
  CutSurfaceDisplay = 1
  Direction = (0,-1,0)
  FileGeomPattern = <path>
  Focus = 100
  FuseBeforeCut = false
  HardHidden = false
  HatchScale = 1
  IsoCount = 0
  IsoHidden = false
  IsoVisible = false
  LockPosition = false
  NameGeomPattern = Diamond
  Perspective = false
  Rotation = 0
  ScaleType = 0
  SeamHidden = false
  SeamVisible = false
  SectionDirection = 2
  SectionNormal = (0,-1,0)
  SectionOrigin = (0,1.5,0)
  SectionSymbol = A
  SmoothHidden = false
  SmoothVisible = true
  Source = -> [Part]
  X = 155.969
  XDirection = (1,0,0)
  Y = 141.934
FEATURE [TechDraw::DrawSVGTemplate] Template001  label="Template_Drawing_ThermalFoil"
  EditableTexts = Designed_by_Name=Stefan Krüger; Drawing_number=2; FC-Date=18.01.2018; FC-SC=1:1; FC-SH=1; FC-Title=LEDBoard 4x4 16bit; Subtitle=HeatSink - ThermalFoil; Weight=-; extra_information_title=URL; extra_information_value=https://github.com/<owner>/LEDBoard_4x4_16bit
  Height = 210
  Orientation = 1
  Width = 297
FEATURE [TechDraw::DrawViewPart] View
  CoarseView = false
  Direction = (0,0,1)
  Focus = 100
  HardHidden = false
  IsoCount = 0
  IsoHidden = false
  IsoVisible = false
  LockPosition = false
  Perspective = false
  Rotation = 0
  ScaleType = 0
  SeamHidden = false
  SeamVisible = false
  SmoothHidden = false
  SmoothVisible = false
  Source = -> [Part001]
  X = 96.2866
  XDirection = (1,0,0)
  Y = 125.096
FEATURE [TechDraw::DrawViewDimension] Dimension009
  Arbitrary = false
  FormatSpec = %.3f
  Inverted = false
  LockPosition = false
  MeasureType = 1
  OverTolerance = 0
  References2D = -> [View]
  Rotation = 0
  ScaleType = 0
  TheoreticalExact = false
  Type = 1
  UnderTolerance = 0
  X = 2.88904
  Y = 23.6626
FEATURE [TechDraw::DrawViewDimension] Dimension010
  Arbitrary = false
  FormatSpec = %.3f
  Inverted = false
  LockPosition = false
  MeasureType = 1
  OverTolerance = 0
  References2D = -> [View]
  Rotation = 0
  ScaleType = 0
  TheoreticalExact = false
  Type = 1
  UnderTolerance = 0
  X = 0.550294
  Y = 7.56654
FEATURE [TechDraw::DrawViewDimension] Dimension011
  Arbitrary = false
  FormatSpec = %.3f
  Inverted = false
  LockPosition = false
  MeasureType = 1
  OverTolerance = 0
  References2D = -> [View]
  Rotation = 0
  ScaleType = 0
  TheoreticalExact = false
  Type = 2
  UnderTolerance = 0
  X = -33.9157
  Y = 18.7253
FEATURE [TechDraw::DrawViewDimension] Dimension012
  Arbitrary = false
  FormatSpec = %.3f
  Inverted = false
  LockPosition = false
  MeasureType = 1
  OverTolerance = 0
  References2D = -> [View]
  Rotation = 0
  ScaleType = 0
  TheoreticalExact = false
  Type = 1
  UnderTolerance = 0
  X = 6.97421
  Y = -29.8076
FEATURE [TechDraw::DrawViewDimension] Dimension013
  Arbitrary = false
  FormatSpec = %.3f
  Inverted = false
  LockPosition = false
  MeasureType = 1
  OverTolerance = 0
  References2D = -> [View]
  Rotation = 0
  ScaleType = 0
  TheoreticalExact = false
  Type = 5
  UnderTolerance = 0
  X = 33.2313
  Y = -3.36014
FEATURE [TechDraw::DrawPage] Page  label="Drawing_ThermalFoil"
  KeepUpdated = true
  NextBalloonIndex = 1
  ProjectionType = 0
  Template = -> Template001
  Views = -> [View,Dimension009,Dimension010,Dimension011,Dimension012,Dimension013]
FEATURE [PartDesign::FeatureBase] Clone  label="Body_Spacer_Hex_M3x15_Clone"
  BaseFeature = -> Body002
  Placement = pos=(10,0,3.3) rot=(0,0,1;0rad)
FEATURE [App::Part] Part003  label="Spacer_Hex_M3x15_CLONE"
  Group = -> [Clone]
  License = CC BY 3.0
  LicenseURL = http://creativecommons.org/licenses/by/3.0/
  Origin = -> Origin006
FEATURE [TechDraw::DrawViewDimension] Dimension
  Arbitrary = false
  FormatSpec = ⌀%.2f
  Inverted = false
  LockPosition = false
  MeasureType = 1
  OverTolerance = 0
  References2D = -> [ProjItem003]
  Rotation = 0
  ScaleType = 0
  TheoreticalExact = false
  Type = 5
  UnderTolerance = 0
  X = -29.8376
  Y = 19.6349
FEATURE [TechDraw::DrawViewImage] Image
  Height = 100
  ImageFile = <userpath>/mydata/github/LEDBoard/LEDBoard_4x4_16bit/parts/mechanical/HeatSink_wSpacer.png
  LockPosition = false
  Rotation = 0
  ScaleType = 2
  Width = 100
  X = 232.745
  Y = 141.781
FEATURE [TechDraw::DrawViewDimension] Dimension014
  Arbitrary = false
  FormatSpec = ⌀%.2f
  Inverted = false
  LockPosition = false
  MeasureType = 1
  OverTolerance = 0
  References2D = -> [ProjItem003]
  Rotation = 0
  ScaleType = 0
  TheoreticalExact = false
  Type = 5
  UnderTolerance = 0
  X = 30.0711
  Y = 19.4305
FEATURE [TechDraw::DrawPage] Page002  label="Drawing_LEDBoard_4x4_16bit_HeatSink"
  KeepUpdated = true
  NextBalloonIndex = 1
  ProjectionType = 0
  Template = -> Template
  Views = -> [ProjGroup,Annotation,Annotation002,Dimension005,Dimension006,Dimension007,Dimension008,Section,Dimension,Image,Dimension014]
note: 1 file-system path scrubbed to <path> (originals preserved in the JSON sidecar)
